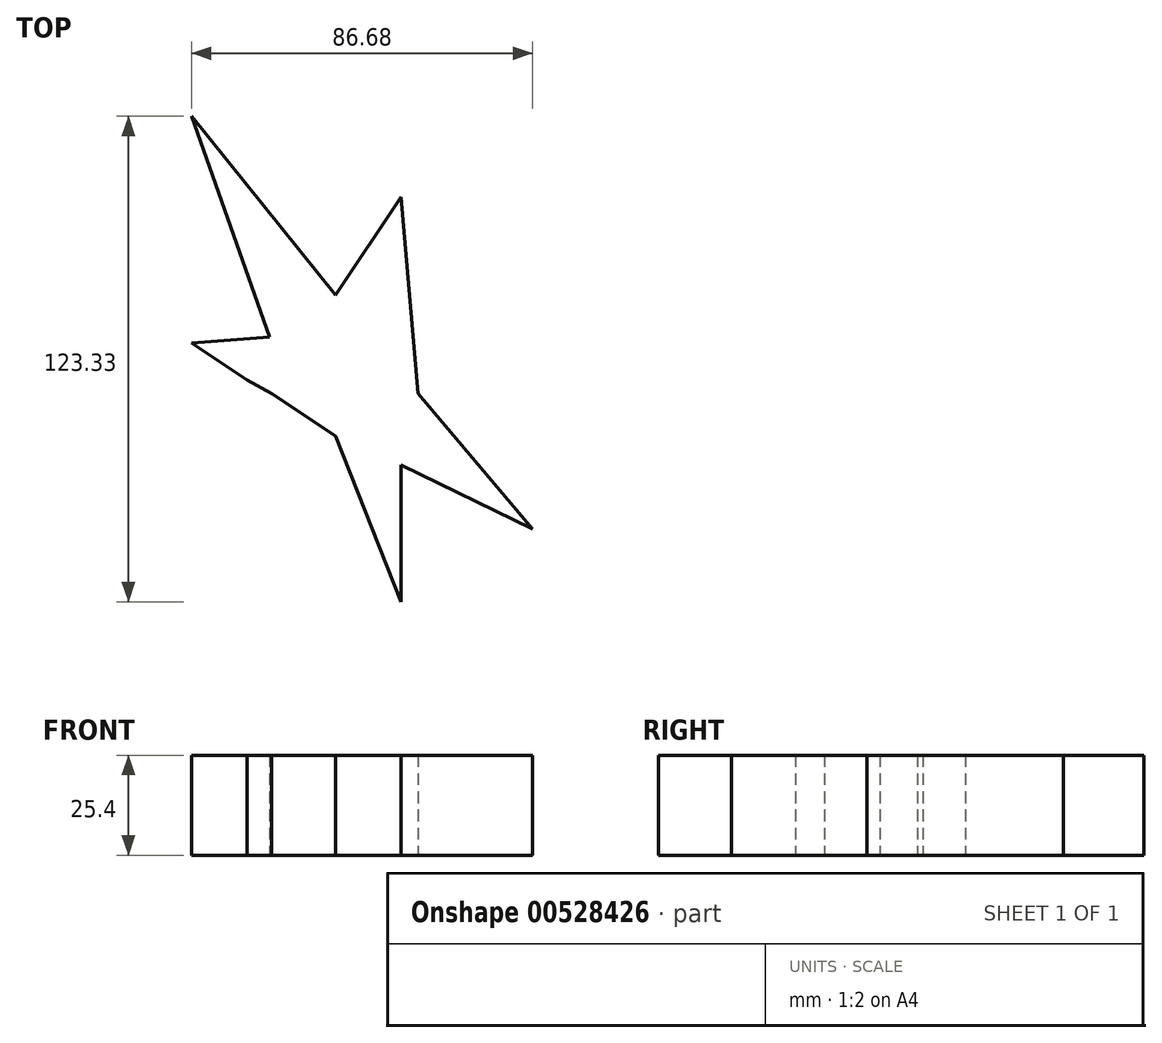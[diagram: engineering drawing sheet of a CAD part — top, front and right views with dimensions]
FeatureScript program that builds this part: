
annotation { "Feature Type Name" : "Feature", "Feature Type Description" : "" }
export const myFeature = defineFeature(function(context is Context, id is Id, definition is map)
    precondition{}
    {
        {
            var Q0;
            Q0=qCreatedBy(makeId("Top.planeOp"),FACE);
            var sketch = newSketch(context, id + "F0", { "sketchPlane" : qUnion([Q0])});
            skLineSegment(sketch, "E0", {"start": v(-196.97, -140.43) * mm, "end": v(-216.84, -84.3) * mm});
            skLineSegment(sketch, "E1", {"start": v(-216.84, -84.3) * mm, "end": v(-180.27, -129.7) * mm});
            skLineSegment(sketch, "E2", {"start": v(-180.27, -129.7) * mm, "end": v(-163.57, -104.8) * mm});
            skLineSegment(sketch, "E3", {"start": v(-163.57, -104.8) * mm, "end": v(-159.3, -154.67) * mm});
            skLineSegment(sketch, "E4", {"start": v(-159.3, -154.67) * mm, "end": v(-130.16, -189.1) * mm});
            skLineSegment(sketch, "E5", {"start": v(-130.16, -189.1) * mm, "end": v(-163.57, -172.86) * mm});
            skLineSegment(sketch, "E6", {"start": v(-163.57, -172.86) * mm, "end": v(-163.57, -207.63) * mm});
            skLineSegment(sketch, "E7", {"start": v(-163.57, -207.63) * mm, "end": v(-180.27, -165.53) * mm});
            skLineSegment(sketch, "E8", {"start": v(-180.27, -165.53) * mm, "end": v(-196.46, -154.67) * mm});
            skLineSegment(sketch, "E9", {"start": v(-202.66, -151.35) * mm, "end": v(-196.46, -154.67) * mm});
            skLineSegment(sketch, "E10", {"start": v(-202.66, -151.35) * mm, "end": v(-216.84, -141.85) * mm});
            skLineSegment(sketch, "E11", {"start": v(-216.84, -141.85) * mm, "end": v(-196.97, -140.43) * mm});
            skSolve(sketch);
        }
        {
            var Q0;
            Q0=makeQuery(id+"F0.imprint","IMPRINT",FACE,{"disambiguationData":[TD([[makeQuery(id+"F0.imprint","IMPRINT",EDGE,{"derivedFrom":sQuery(id+"F0.wireOp",EDGE,"E0")}),-1.0]])]});
            extrude(context, id + "F1", {"entities" : qUnion([Q0]), "depth" : 25.4 * mm, "offsetDistance" : 25.4 * mm});
        }
    });
